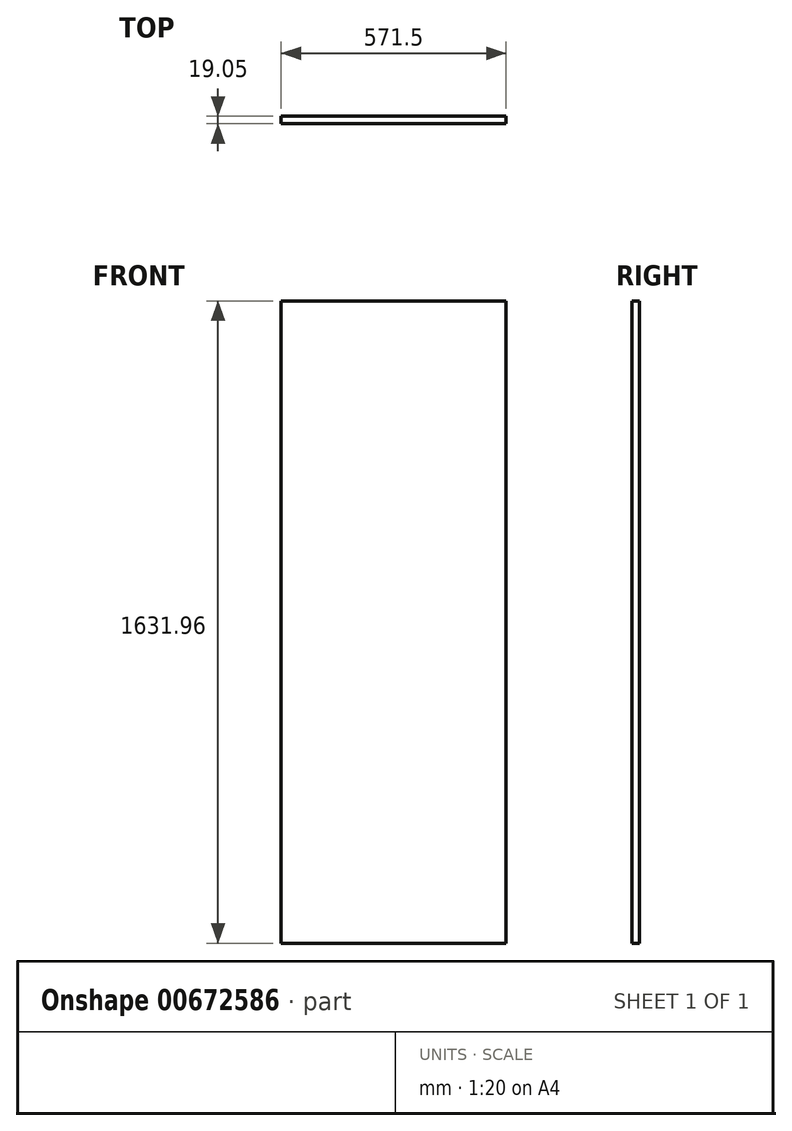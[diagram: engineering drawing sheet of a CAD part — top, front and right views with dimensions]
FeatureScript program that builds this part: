
annotation { "Feature Type Name" : "Feature", "Feature Type Description" : "" }
export const myFeature = defineFeature(function(context is Context, id is Id, definition is map)
    precondition{}
    {
        {
            var Q0;
            Q0=qCreatedBy(makeId("Front.planeOp"),FACE);
            var sketch = newSketch(context, id + "F0", { "sketchPlane" : qUnion([Q0])});
            skLineSegment(sketch, "E0.bottom", {"start": v(285.75, 815.98) * mm, "end": v(-285.75, 815.98) * mm});
            skLineSegment(sketch, "E0.top", {"start": v(285.75, -815.98) * mm, "end": v(-285.75, -815.98) * mm});
            skLineSegment(sketch, "E0.left", {"start": v(285.75, 815.98) * mm, "end": v(285.75, -815.98) * mm});
            skLineSegment(sketch, "E0.right", {"start": v(-285.75, 815.98) * mm, "end": v(-285.75, -815.98) * mm});
            skPoint(sketch, "E0.middle", {"position": v(0, 0) * mm});
            skSolve(sketch);
        }
        {
            var Q0;
            Q0=makeQuery(id+"F0.imprint","IMPRINT",FACE,{"disambiguationData":[TD([[makeQuery(id+"F0.imprint","IMPRINT",EDGE,{"derivedFrom":sQuery(id+"F0.wireOp",EDGE,"E0.bottom")}),1.0]])]});
            extrude(context, id + "F1", {"entities" : qUnion([Q0]), "depth" : 19.05 * mm, "offsetDistance" : 25.4 * mm});
        }
    });
